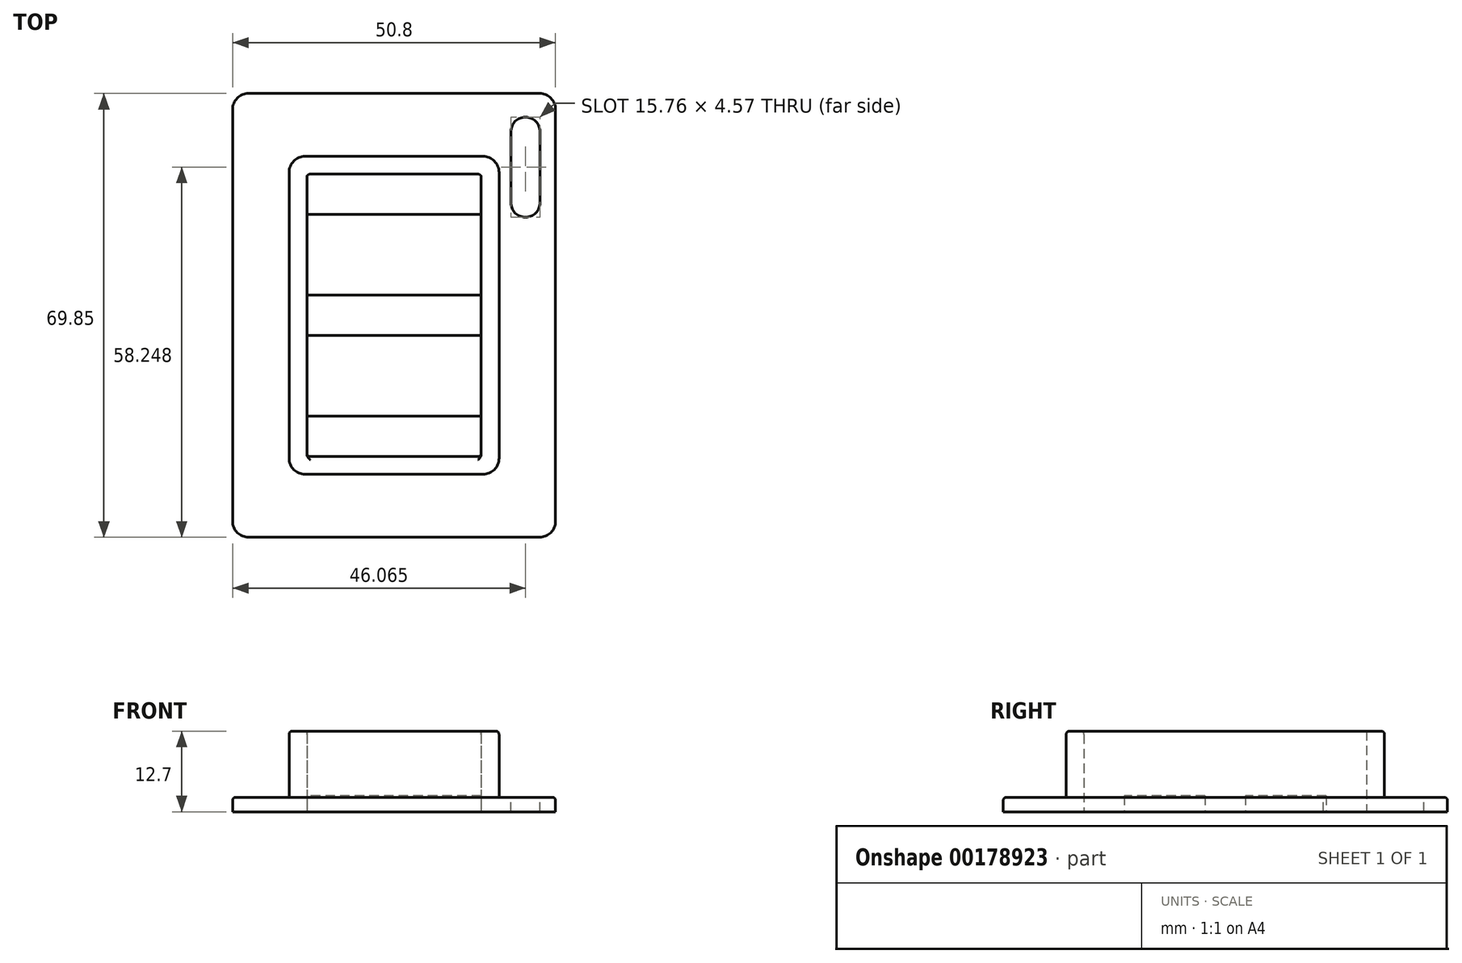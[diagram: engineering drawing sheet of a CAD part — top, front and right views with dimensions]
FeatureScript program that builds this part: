
annotation { "Feature Type Name" : "Feature", "Feature Type Description" : "" }
export const myFeature = defineFeature(function(context is Context, id is Id, definition is map)
    precondition{}
    {
        {
            var Q0;
            Q0=qCreatedBy(makeId("Top.planeOp"),FACE);
            var sketch = newSketch(context, id + "F0", { "sketchPlane" : qUnion([Q0])});
            skLineSegment(sketch, "E0.bottom", {"start": v(-30.33, 2.47) * mm, "end": v(2.7, 2.47) * mm});
            skLineSegment(sketch, "E0.top", {"start": v(-30.33, -47.57) * mm, "end": v(2.7, -47.57) * mm});
            skLineSegment(sketch, "E0.left", {"start": v(-30.33, 2.47) * mm, "end": v(-30.33, -47.57) * mm});
            skLineSegment(sketch, "E0.right", {"start": v(2.7, 2.47) * mm, "end": v(2.7, -47.57) * mm});
            skLineSegment(sketch, "E1.0", {"start": v(-27.54, -44.78) * mm, "end": v(-0.1, -44.78) * mm});
            skLineSegment(sketch, "E1.1", {"start": v(-27.54, -0.33) * mm, "end": v(-27.54, -44.78) * mm});
            skLineSegment(sketch, "E1.2", {"start": v(-27.54, -0.33) * mm, "end": v(-0.1, -0.33) * mm});
            skLineSegment(sketch, "E1.3", {"start": v(-0.1, -0.33) * mm, "end": v(-0.1, -44.78) * mm});
            skLineSegment(sketch, "E2.bottom", {"start": v(-39.22, 12.37) * mm, "end": v(11.58, 12.37) * mm});
            skLineSegment(sketch, "E2.top", {"start": v(-39.22, -57.48) * mm, "end": v(11.58, -57.48) * mm});
            skLineSegment(sketch, "E2.left", {"start": v(-39.22, 12.37) * mm, "end": v(-39.22, -57.48) * mm});
            skLineSegment(sketch, "E2.right", {"start": v(11.58, 12.37) * mm, "end": v(11.58, -57.48) * mm});
            skSolve(sketch);
        }
        {
            var Q0;
            Q0=makeQuery(id+"F0.imprint","IMPRINT",FACE,{"disambiguationData":[TD([[makeQuery(id+"F0.imprint","IMPRINT",EDGE,{"derivedFrom":sQuery(id+"F0.wireOp",EDGE,"E0.bottom")}),-1.0]])]});
            extrude(context, id + "F1", {"entities" : qUnion([Q0]), "depth" : 12.7 * mm});
        }
        {
            var Q0;
            Q0 = qSketchRegion(id + "F0", true);
            extrude(context, id + "F2", {"entities" : qUnion([Q0]), "operationType" : NewBodyOperationType.ADD, "depth" : 2.3 * mm});
        }
        {
            var Q0;
            {var subQ0=sQuery(id+"F0.wireOp",EDGE,"E0.right");var subQ1=sQuery(id+"F0.wireOp",EDGE,"E0.left");var subQ2=sQuery(id+"F0.wireOp",EDGE,"E0.top");var subQ3=sQuery(id+"F0.wireOp",EDGE,"E0.bottom");Q0=makeQuery(id+"F2.boolean.opBoolean","MERGE",FACE,{"derivedFrom":[makeQuery(id+"F1.opExtrude","CAP_FACE",FACE,{"disambiguationData":[OSD([subQ3,subQ2,subQ1,subQ0,sQuery(id+"F0.wireOp",EDGE,"E1.0"),sQuery(id+"F0.wireOp",EDGE,"E1.1"),sQuery(id+"F0.wireOp",EDGE,"E1.2"),sQuery(id+"F0.wireOp",EDGE,"E1.3")])],"isStart":true}),makeQuery(id+"F2.opExtrude","CAP_FACE",FACE,{"disambiguationData":[OSD([subQ3,subQ2,subQ1,subQ0,sQuery(id+"F0.wireOp",EDGE,"E2.bottom"),sQuery(id+"F0.wireOp",EDGE,"E2.top"),sQuery(id+"F0.wireOp",EDGE,"E2.left"),sQuery(id+"F0.wireOp",EDGE,"E2.right")])],"isStart":true})]});}
            var sketch = newSketch(context, id + "F3", { "sketchPlane" : qUnion([Q0])});
            skLineSegment(sketch, "E3", {"start": v(-0.1, 38.43) * mm, "end": v(-27.54, 38.43) * mm});
            skLineSegment(sketch, "E4", {"start": v(-0.1, 25.73) * mm, "end": v(-27.54, 25.73) * mm});
            skLineSegment(sketch, "E5", {"start": v(-0.1, 6.68) * mm, "end": v(-27.54, 6.68) * mm});
            skLineSegment(sketch, "E6", {"start": v(-0.1, 19.38) * mm, "end": v(-27.54, 19.38) * mm});
            skSolve(sketch);
        }
        {
            var Q0;
            Q0 = qSketchRegion(id + "F3", true);
            var Q1;
            {var subQ0=sQuery(id+"F3.wireOp",EDGE,"E3");Q1=makeQuery(id+"F3.imprint","IMPRINT",FACE,{"disambiguationData":[TD([[makeQuery(id+"F3.imprint","IMPRINT",EDGE,{"derivedFrom":subQ0}),1.0]])]});}
            var Q2;
            {var subQ0=sQuery(id+"F3.wireOp",EDGE,"E5");Q2=makeQuery(id+"F3.imprint","IMPRINT",FACE,{"disambiguationData":[TD([[makeQuery(id+"F3.imprint","IMPRINT",EDGE,{"derivedFrom":subQ0}),-1.0]])]});}
            extrude(context, id + "F4", {"entities" : qUnion([Q0, Q1, Q2]), "oppositeDirection" : true, "depth" : 2.54 * mm});
        }
        {
            var Q0;
            Q0=makeQuery(id+"F1.opExtrude","SWEPT_EDGE",EDGE,{"disambiguationData":[OSD([sQuery(id+"F0.wireOp",EDGE,"E0.bottom"),sQuery(id+"F0.wireOp",EDGE,"E0.right")])]});
            var Q1;
            Q1=makeQuery(id+"F1.opExtrude","SWEPT_EDGE",EDGE,{"disambiguationData":[OSD([sQuery(id+"F0.wireOp",EDGE,"E0.top"),sQuery(id+"F0.wireOp",EDGE,"E0.right")])]});
            var Q2;
            Q2=makeQuery(id+"F1.opExtrude","SWEPT_EDGE",EDGE,{"disambiguationData":[OSD([sQuery(id+"F0.wireOp",EDGE,"E0.bottom"),sQuery(id+"F0.wireOp",EDGE,"E0.left")])]});
            var Q3;
            Q3=makeQuery(id+"F1.opExtrude","SWEPT_EDGE",EDGE,{"disambiguationData":[OSD([sQuery(id+"F0.wireOp",EDGE,"E0.top"),sQuery(id+"F0.wireOp",EDGE,"E0.left")])]});
            fillet(context, id + "F5", {"entities" : qUnion([Q0, Q1, Q2, Q3]), "radius" : 2.54 * mm, "tangentPropagation" : true, "allowEdgeOverflow" : false});
        }
        {
            var Q0;
            Q0=makeQuery(id+"F2.opExtrude","SWEPT_EDGE",EDGE,{"disambiguationData":[OSD([sQuery(id+"F0.wireOp",EDGE,"E2.bottom"),sQuery(id+"F0.wireOp",EDGE,"E2.right")])]});
            var Q1;
            Q1=makeQuery(id+"F2.opExtrude","SWEPT_EDGE",EDGE,{"disambiguationData":[OSD([sQuery(id+"F0.wireOp",EDGE,"E2.top"),sQuery(id+"F0.wireOp",EDGE,"E2.right")])]});
            var Q2;
            Q2=makeQuery(id+"F2.opExtrude","SWEPT_EDGE",EDGE,{"disambiguationData":[OSD([sQuery(id+"F0.wireOp",EDGE,"E2.top"),sQuery(id+"F0.wireOp",EDGE,"E2.left")])]});
            var Q3;
            Q3=makeQuery(id+"F2.opExtrude","SWEPT_EDGE",EDGE,{"disambiguationData":[OSD([sQuery(id+"F0.wireOp",EDGE,"E2.bottom"),sQuery(id+"F0.wireOp",EDGE,"E2.left")])]});
            fillet(context, id + "F6", {"entities" : qUnion([Q0, Q1, Q2, Q3]), "radius" : 2.54 * mm, "tangentPropagation" : true, "allowEdgeOverflow" : false});
        }
        {
            var Q0;
            Q0=makeQuery(id+"F2.opExtrude","CAP_EDGE",EDGE,{"disambiguationData":[OSD([sQuery(id+"F0.wireOp",EDGE,"E0.left")])],"isStart":false});
            var Q1;
            Q1=makeQuery(id+"F2.opExtrude","CAP_EDGE",EDGE,{"disambiguationData":[OSD([sQuery(id+"F0.wireOp",EDGE,"E2.left")])],"isStart":false});
            var Q2;
            Q2=makeQuery(id+"F9bNHF4t5X5IWEJ_3.boolean.opBoolean","COPY",EDGE,{"derivedFrom":makeQuery(id+"F9bNHF4t5X5IWEJ_3.opExtrude","CAP_EDGE",EDGE,{"disambiguationData":[OSD([sQuery(id+"F2VEfHODBBdV9Hi_3.wireOp",EDGE,"jVNs46VV-RurV-fgns-MeVl-wpwwu6KExGYe.top")])],"isStart":true})});
            var Q3;
            Q3=makeQuery(id+"F9bNHF4t5X5IWEJ_3.boolean.opBoolean","COPY",EDGE,{"derivedFrom":makeQuery(id+"F9bNHF4t5X5IWEJ_3.opExtrude","CAP_EDGE",EDGE,{"disambiguationData":[OSD([sQuery(id+"F2VEfHODBBdV9Hi_3.wireOp",EDGE,"bL0p9bzn-Fpqf-GdXD-2uUG-ym66f8d2ubjb.left")])],"isStart":true})});
            var Q4;
            Q4=makeQuery(id+"F1.opExtrude","CAP_EDGE",EDGE,{"disambiguationData":[OSD([sQuery(id+"F0.wireOp",EDGE,"E0.right")])],"isStart":false});
            var Q5;
            Q5=makeQuery(id+"F1.opExtrude","CAP_EDGE",EDGE,{"disambiguationData":[OSD([sQuery(id+"F0.wireOp",EDGE,"E1.0")])],"isStart":false});
            var Q6;
            Q6=makeQuery(id+"F9bNHF4t5X5IWEJ_3.boolean.opBoolean","COPY",EDGE,{"derivedFrom":makeQuery(id+"F9bNHF4t5X5IWEJ_3.opExtrude","CAP_EDGE",EDGE,{"disambiguationData":[OSD([sQuery(id+"F2VEfHODBBdV9Hi_3.wireOp",EDGE,"jh6aFYoG-Riae-kP7m-e7lY-x4QIz8OLGlFO.bottom")])],"isStart":true})});
            var Q7;
            Q7=makeQuery(id+"F9bNHF4t5X5IWEJ_3.boolean.opBoolean","COPY",EDGE,{"derivedFrom":makeQuery(id+"F9bNHF4t5X5IWEJ_3.opExtrude","CAP_EDGE",EDGE,{"disambiguationData":[OSD([sQuery(id+"F2VEfHODBBdV9Hi_3.wireOp",EDGE,"A43tenQH-CksE-GDKi-9cBf-9No8C3qe5PJG.bottom")])],"isStart":true})});
            fillet(context, id + "F7", {"entities" : qUnion([Q0, Q1, Q2, Q3, Q4, Q5, Q6, Q7]), "radius" : 0.5 * mm, "tangentPropagation" : true, "allowEdgeOverflow" : false});
        }
        {
            var Q0;
            Q0=makeQuery(id+"F1.opExtrude","SWEPT_EDGE",EDGE,{"disambiguationData":[OSD([sQuery(id+"F0.wireOp",EDGE,"E1.2"),sQuery(id+"F0.wireOp",EDGE,"E1.3")])]});
            var Q1;
            Q1=makeQuery(id+"F1.opExtrude","SWEPT_EDGE",EDGE,{"disambiguationData":[OSD([sQuery(id+"F0.wireOp",EDGE,"E1.0"),sQuery(id+"F0.wireOp",EDGE,"E1.3")])]});
            var Q2;
            Q2=makeQuery(id+"F1.opExtrude","SWEPT_EDGE",EDGE,{"disambiguationData":[OSD([sQuery(id+"F0.wireOp",EDGE,"E1.0"),sQuery(id+"F0.wireOp",EDGE,"E1.1")])]});
            var Q3;
            Q3=makeQuery(id+"F1.opExtrude","SWEPT_EDGE",EDGE,{"disambiguationData":[OSD([sQuery(id+"F0.wireOp",EDGE,"E1.1"),sQuery(id+"F0.wireOp",EDGE,"E1.2")])]});
            fillet(context, id + "F8", {"entities" : qUnion([Q0, Q1, Q2, Q3]), "radius" : 0.5 * mm, "tangentPropagation" : true, "allowEdgeOverflow" : false});
        }
        {
            var Q0;
            Q0=makeQuery(id+"F2.opExtrude","CAP_FACE",FACE,{"disambiguationData":[OSD([sQuery(id+"F0.wireOp",EDGE,"E0.bottom"),sQuery(id+"F0.wireOp",EDGE,"E0.top"),sQuery(id+"F0.wireOp",EDGE,"E0.left"),sQuery(id+"F0.wireOp",EDGE,"E0.right"),sQuery(id+"F0.wireOp",EDGE,"E2.bottom"),sQuery(id+"F0.wireOp",EDGE,"E2.top"),sQuery(id+"F0.wireOp",EDGE,"E2.left"),sQuery(id+"F0.wireOp",EDGE,"E2.right")])],"isStart":false});
            var sketch = newSketch(context, id + "F9", { "sketchPlane" : qUnion([Q0])});
            skLineSegment(sketch, "E7.left", {"start": v(4.56, 6.36) * mm, "end": v(4.56, -4.82) * mm});
            skLineSegment(sketch, "E7.right", {"start": v(9.13, 6.36) * mm, "end": v(9.13, -4.82) * mm});
            skArc(sketch, "E8", {"start": v(9.13, 6.36) * mm, "mid": v(6.84, 8.65) * mm, "end": v(4.56, 6.36) * mm});
            skArc(sketch, "E9", {"start": v(4.56, -4.82) * mm, "mid": v(6.84, -7.11) * mm, "end": v(9.13, -4.82) * mm});
            skSolve(sketch);
        }
        {
            var Q0;
            Q0=makeQuery(id+"F9.imprint","IMPRINT",FACE,{"disambiguationData":[TD([[makeQuery(id+"F9.imprint","IMPRINT",EDGE,{"derivedFrom":sQuery(id+"F9.wireOp",EDGE,"E7.left")}),1.0]])]});
            extrude(context, id + "F10", {"entities" : qUnion([Q0]), "operationType" : NewBodyOperationType.REMOVE, "endBound" : BoundingType.THROUGH_ALL, "oppositeDirection" : true, "depth" : 25.4 * mm});
        }
    });
